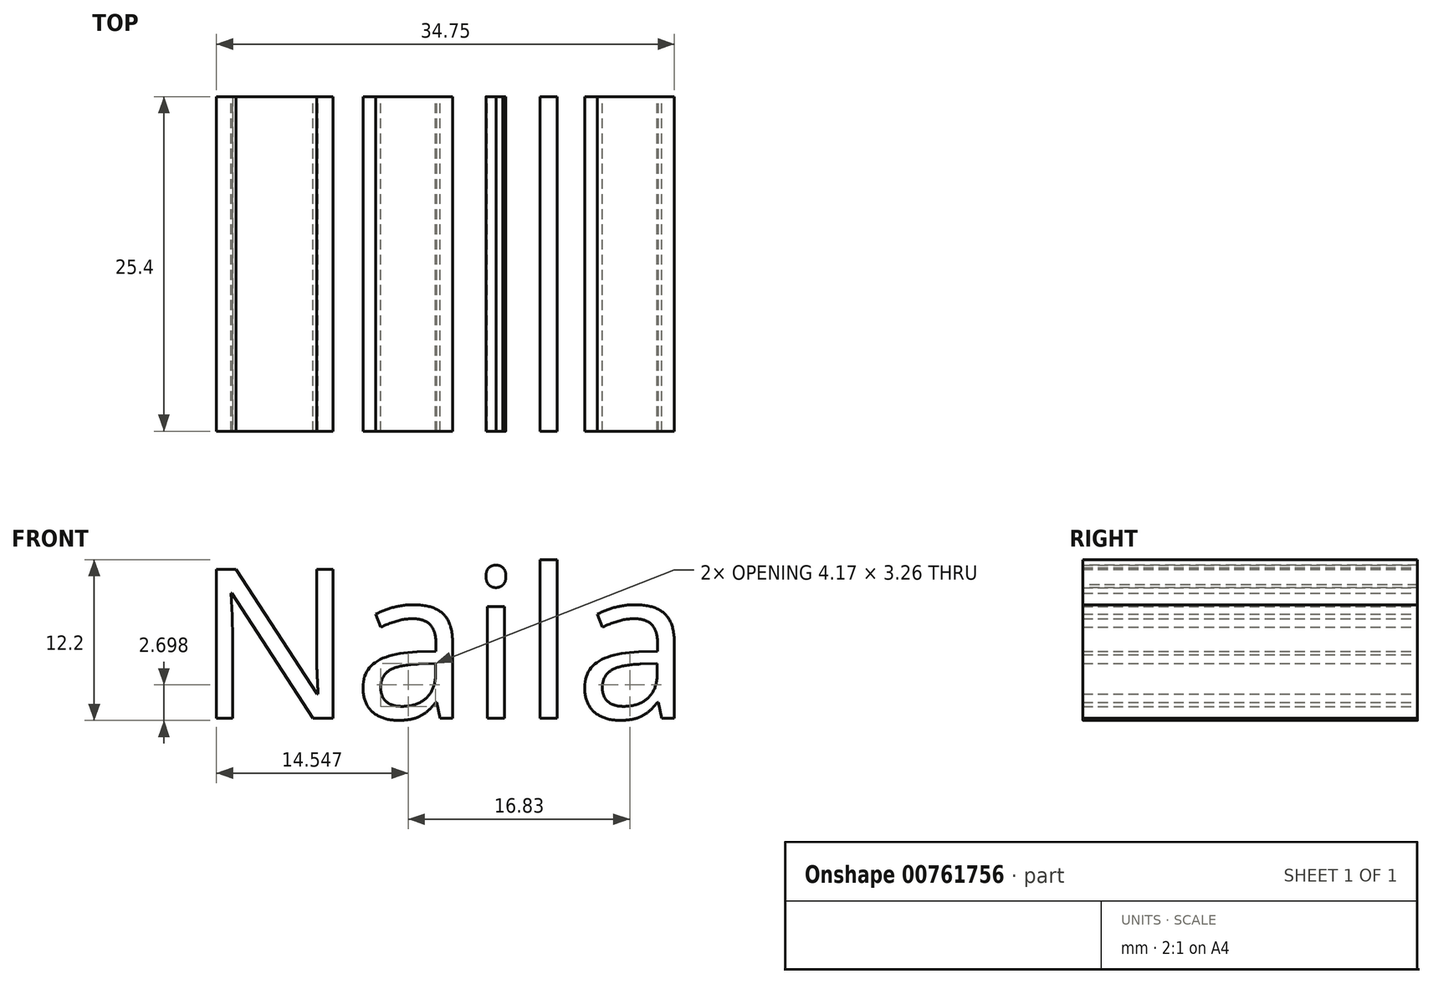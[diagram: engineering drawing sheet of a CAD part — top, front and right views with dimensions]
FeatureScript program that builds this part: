
annotation { "Feature Type Name" : "Feature", "Feature Type Description" : "" }
export const myFeature = defineFeature(function(context is Context, id is Id, definition is map)
    precondition{}
    {
        {
            var Q0;
            Q0=qCreatedBy(makeId("Front.planeOp"),FACE);
            var sketch = newSketch(context, id + "F0", { "sketchPlane" : qUnion([Q0])});
            skText(sketch, "E0", { "text": "Naila", "fontName": "OpenSans-Regular.ttf"});
            const initialGuessF0  = {"E0": [-0.03734, 0, 1, 0, 0.01141]};
            skSetInitialGuess(sketch, initialGuessF0);
            skSolve(sketch);
        }
        {
            var Q0;
            Q0 = qSketchRegion(id + "F0", true);
            extrude(context, id + "F1", {"entities" : qUnion([Q0]), "depth" : 25.4 * mm, "offsetDistance" : 25.4 * mm});
        }
    });
